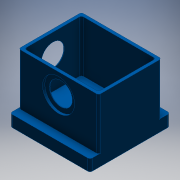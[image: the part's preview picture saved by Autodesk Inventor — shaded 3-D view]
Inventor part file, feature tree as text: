
AUTODESK INVENTOR PART (.ipt)
format: ipt  version: 2016 (Build 200138000, 138)  size: 192,512 bytes
history: native  units: mm
features: extrude x6, sketch x6
ambient origin geometry x8: Origin, YZ Plane, XZ Plane, XY Plane, X Axis, Y Axis, Z Axis, Center Point
bodies: Solid1 (feature_tree)
feature tree (12):
  extrude  "Extrusion1"  Depth=70.0mm
  extrude  "Extrusion2"  Depth=70.0mm
  extrude  "Extrusion8"  Depth=70.0mm
  extrude  "Extrusion9"  Depth=55.0mm
  extrude  "Extrusion12"  Depth=2.5mm
  extrude  "Extrusion13"  Depth=2.5mm
  sketch  "Sketch1"  dims[d0=70.0mm d1=35.0mm]
  sketch  "Sketch3"  dims[d2=70.0mm d3=35.0mm]
  sketch  "Sketch9"  dims[d4=10.0mm d5=0.0mm d17=70.0mm]
  sketch  "Sketch10"  dims[d18=55.0mm d19=27.5mm]
  sketch  "Sketch13"  dims[d20=2.5mm d21=2.5mm]
  sketch  "Sketch14"  dims[d22=2.5mm d23=2.5mm d24=45.0mm d25=0.0mm d60=28.0mm d61=35.0mm d62=27.5mm d63=2.0mm d64=0.0mm d65=20.0mm d66=2.0mm d67=0.0mm d76=28.0mm d78=2.0mm d79=0.0mm d80=20.0mm d81=27.5mm d82=27.5mm d83=2.0mm d84=0.0mm d85=2.0mm d86=2.0mm]
